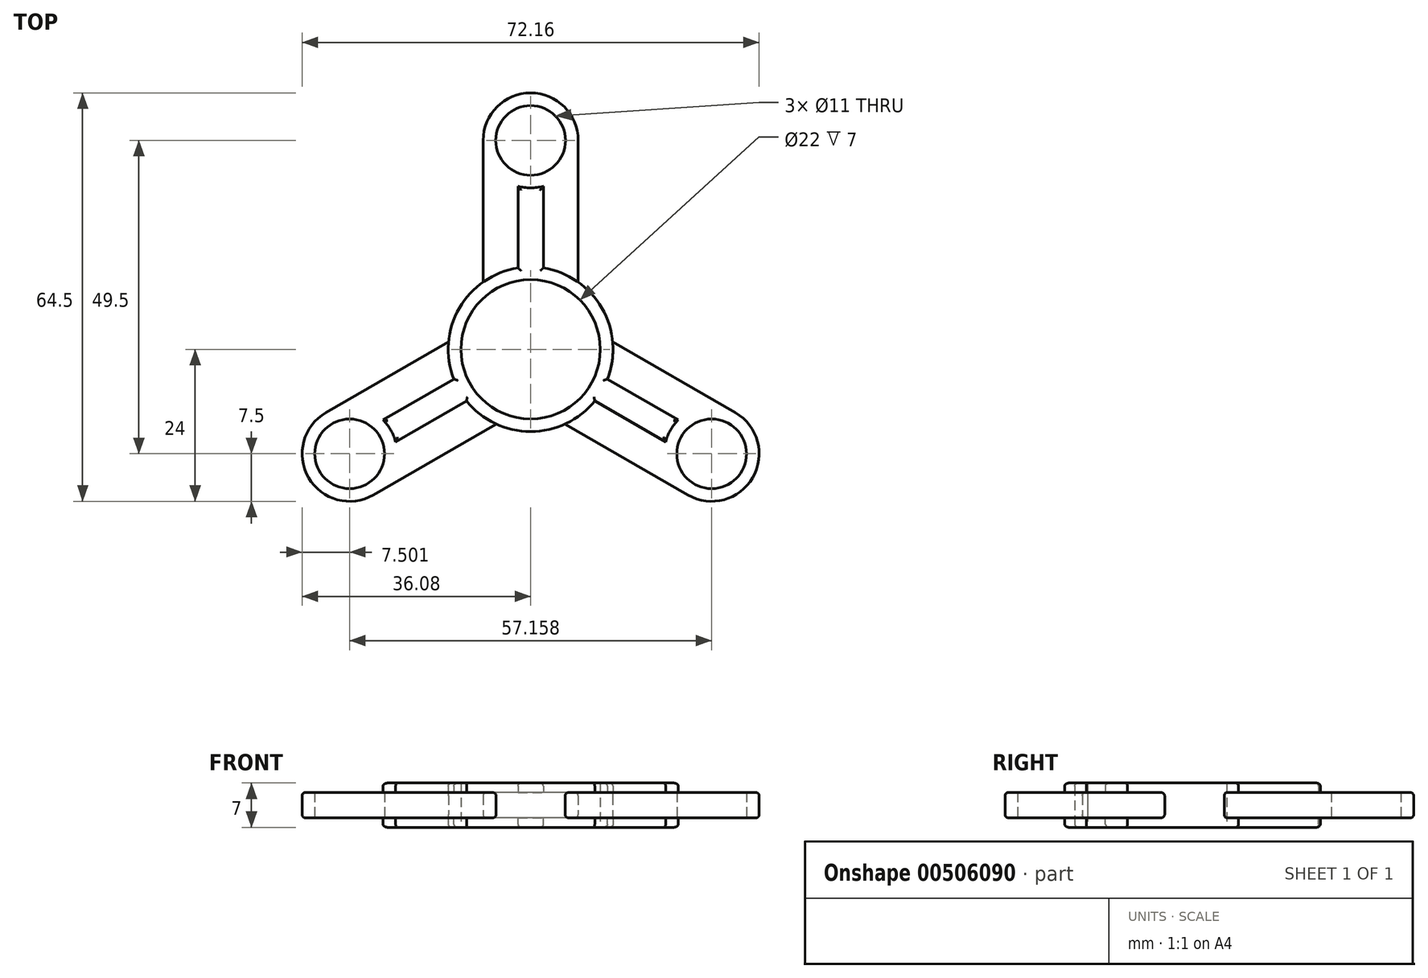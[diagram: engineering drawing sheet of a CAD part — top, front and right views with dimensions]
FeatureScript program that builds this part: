
annotation { "Feature Type Name" : "Feature", "Feature Type Description" : "" }
export const myFeature = defineFeature(function(context is Context, id is Id, definition is map)
    precondition{}
    {
        {
            var Q0;
            Q0=qCreatedBy(makeId("Top.planeOp"),FACE);
            var sketch = newSketch(context, id + "F0", { "sketchPlane" : qUnion([Q0])});
            skCircle(sketch, "E0", {"center": v(0, 0) * mm, "radius": 11 * mm});
            skCircle(sketch, "E1", {"center": v(0, 33) * mm, "radius": 5.5 * mm});
            skCircle(sketch, "E2", {"center": v(-28.58, -16.5) * mm, "radius": 5.5 * mm});
            skCircle(sketch, "E3", {"center": v(28.58, -16.5) * mm, "radius": 5.5 * mm});
            skCircle(sketch, "E4", {"center": v(0, 33) * mm, "radius": 7.5 * mm});
            skCircle(sketch, "E5", {"center": v(-28.58, -16.5) * mm, "radius": 7.5 * mm});
            skCircle(sketch, "E6", {"center": v(28.58, -16.5) * mm, "radius": 7.5 * mm});
            skCircle(sketch, "E7", {"center": v(0, 0) * mm, "radius": 13 * mm});
            skLineSegment(sketch, "E8", {"start": v(-7.5, 33) * mm, "end": v(-7.5, 10.62) * mm});
            skLineSegment(sketch, "E9", {"start": v(7.5, 33) * mm, "end": v(7.5, 10.62) * mm});
            skLineSegment(sketch, "E10", {"start": v(32.33, -10) * mm, "end": v(12.95, 1.19) * mm});
            skLineSegment(sketch, "E11", {"start": v(24.83, -23) * mm, "end": v(5.45, -11.8) * mm});
            skLineSegment(sketch, "E12", {"start": v(-32.33, -10) * mm, "end": v(-12.95, 1.19) * mm});
            skLineSegment(sketch, "E13", {"start": v(-24.83, -23) * mm, "end": v(-5.45, -11.8) * mm});
            skLineSegment(sketch, "E14", {"start": v(-12.12, -4.7) * mm, "end": v(-23.32, -11.15) * mm});
            skLineSegment(sketch, "E15", {"start": v(-10.12, -8.15) * mm, "end": v(-21.32, -14.62) * mm});
            skLineSegment(sketch, "E16", {"start": v(12.12, -4.7) * mm, "end": v(23.32, -11.15) * mm});
            skLineSegment(sketch, "E17", {"start": v(21.32, -14.62) * mm, "end": v(10.12, -8.15) * mm});
            skLineSegment(sketch, "E18", {"start": v(-2, 25.77) * mm, "end": v(-2, 12.85) * mm});
            skLineSegment(sketch, "E19", {"start": v(2, 25.77) * mm, "end": v(2, 12.85) * mm});
            skSolve(sketch);
        }
        {
            var Q0;
            Q0=qSketchRegion(id+"F0",true);
            extrude(context, id + "F1", {"entities" : qUnion([Q0]), "depth" : 4 * mm});
        }
        {
            var Q0;
            {var subQ0=sQuery(id+"F0.wireOp",EDGE,"E14");Q0=makeQuery(id+"F0.imprint","IMPRINT",FACE,{"disambiguationData":[TD([[makeQuery(id+"F0.imprint","IMPRINT",EDGE,{"derivedFrom":subQ0}),1.0]])]});}
            var Q1;
            {var subQ0=sQuery(id+"F0.wireOp",EDGE,"E18");Q1=makeQuery(id+"F0.imprint","IMPRINT",FACE,{"disambiguationData":[TD([[makeQuery(id+"F0.imprint","IMPRINT",EDGE,{"derivedFrom":subQ0}),1.0]])]});}
            var Q2;
            {var subQ0=sQuery(id+"F0.wireOp",EDGE,"E16");Q2=makeQuery(id+"F0.imprint","IMPRINT",FACE,{"disambiguationData":[TD([[makeQuery(id+"F0.imprint","IMPRINT",EDGE,{"derivedFrom":subQ0}),-1.0]])]});}
            var Q3;
            Q3=makeQuery(id+"F0.imprint","IMPRINT",FACE,{"disambiguationData":[TD([[makeQuery(id+"F0.imprint","IMPRINT",EDGE,{"derivedFrom":sQuery(id+"F0.wireOp",EDGE,"E0")}),-1.0]])]});
            extrude(context, id + "F2", {"entities" : qUnion([Q0, Q1, Q2, Q3]), "operationType" : NewBodyOperationType.ADD, "depth" : 5.5 * mm});
        }
        {
            var Q0;
            {var subQ0=sQuery(id+"F0.wireOp",EDGE,"E14");Q0=makeQuery(id+"F0.imprint","IMPRINT",FACE,{"disambiguationData":[TD([[makeQuery(id+"F0.imprint","IMPRINT",EDGE,{"derivedFrom":subQ0}),1.0]])]});}
            var Q1;
            Q1=makeQuery(id+"F0.imprint","IMPRINT",FACE,{"disambiguationData":[TD([[makeQuery(id+"F0.imprint","IMPRINT",EDGE,{"derivedFrom":sQuery(id+"F0.wireOp",EDGE,"E0")}),-1.0]])]});
            var Q2;
            {var subQ0=sQuery(id+"F0.wireOp",EDGE,"E18");Q2=makeQuery(id+"F0.imprint","IMPRINT",FACE,{"disambiguationData":[TD([[makeQuery(id+"F0.imprint","IMPRINT",EDGE,{"derivedFrom":subQ0}),1.0]])]});}
            var Q3;
            {var subQ0=sQuery(id+"F0.wireOp",EDGE,"E16");Q3=makeQuery(id+"F0.imprint","IMPRINT",FACE,{"disambiguationData":[TD([[makeQuery(id+"F0.imprint","IMPRINT",EDGE,{"derivedFrom":subQ0}),-1.0]])]});}
            extrude(context, id + "F3", {"entities" : qUnion([Q0, Q1, Q2, Q3]), "operationType" : NewBodyOperationType.ADD, "oppositeDirection" : true, "depth" : 1.5 * mm});
        }
        {
            var Q0;
            Q0=makeQuery(id+"F2.opExtrude","CAP_EDGE",EDGE,{"disambiguationData":[OSD([sQuery(id+"F0.wireOp",EDGE,"E15")])],"isStart":false});
            var Q1;
            Q1=makeQuery(id+"F2.opExtrude","CAP_EDGE",EDGE,{"disambiguationData":[OSD([sQuery(id+"F0.wireOp",EDGE,"E14")])],"isStart":false});
            var Q2;
            Q2=makeQuery(id+"F2.opExtrude","CAP_EDGE",EDGE,{"disambiguationData":[OSD([sQuery(id+"F0.wireOp",EDGE,"E5")])],"isStart":false});
            var Q3;
            Q3=makeQuery(id+"F2.opExtrude","CAP_EDGE",EDGE,{"disambiguationData":[OSD([sQuery(id+"F0.wireOp",EDGE,"E17")])],"isStart":false});
            var Q4;
            Q4=makeQuery(id+"F2.opExtrude","CAP_EDGE",EDGE,{"disambiguationData":[OSD([sQuery(id+"F0.wireOp",EDGE,"E16")])],"isStart":false});
            var Q5;
            Q5=makeQuery(id+"F2.opExtrude","CAP_EDGE",EDGE,{"disambiguationData":[OSD([sQuery(id+"F0.wireOp",EDGE,"E6")])],"isStart":false});
            var Q6;
            Q6=makeQuery(id+"F2.opExtrude","CAP_EDGE",EDGE,{"disambiguationData":[OSD([sQuery(id+"F0.wireOp",EDGE,"E18")])],"isStart":false});
            var Q7;
            Q7=makeQuery(id+"F2.opExtrude","CAP_EDGE",EDGE,{"disambiguationData":[OSD([sQuery(id+"F0.wireOp",EDGE,"E19")])],"isStart":false});
            var Q8;
            Q8=makeQuery(id+"F2.opExtrude","CAP_EDGE",EDGE,{"disambiguationData":[OSD([sQuery(id+"F0.wireOp",EDGE,"E4")])],"isStart":false});
            fillet(context, id + "F4", {"entities" : qUnion([Q0, Q1, Q2, Q3, Q4, Q5, Q6, Q7, Q8]), "radius" : .5 * mm, "tangentPropagation" : true, "allowEdgeOverflow" : false});
        }
        {
            var Q0;
            {var subQ0=sQuery(id+"F0.wireOp",EDGE,"E7");var subQ1=makeQuery(id+"F0.imprint","INTERSECT",VERTEX,{"derivedFrom":[subQ0,sQuery(id+"F0.wireOp",EDGE,"E12")]});var subQ2=makeQuery(id+"F0.imprint","INTERSECT",VERTEX,{"derivedFrom":[subQ0,sQuery(id+"F0.wireOp",EDGE,"E8")]});Q0=makeQuery(id+"F2.opExtrude","CAP_EDGE",EDGE,{"disambiguationData":[OSD([subQ0]),TDD([makeQuery(id+"F0.imprint","IMPRINT",EDGE,{"disambiguationData":[TD([[subQ2,1.0]])],"derivedFrom":subQ0}),makeQuery(id+"F0.imprint","IMPRINT",EDGE,{"disambiguationData":[TD([[subQ2,-1.0]])],"derivedFrom":subQ0}),makeQuery(id+"F0.imprint","IMPRINT",EDGE,{"disambiguationData":[TD([[subQ1,-1.0]])],"derivedFrom":subQ0})])],"isStart":false});}
            var Q1;
            {var subQ0=sQuery(id+"F0.wireOp",EDGE,"E7");var subQ1=makeQuery(id+"F0.imprint","INTERSECT",VERTEX,{"derivedFrom":[subQ0,sQuery(id+"F0.wireOp",EDGE,"E11")]});var subQ2=makeQuery(id+"F0.imprint","INTERSECT",VERTEX,{"derivedFrom":[subQ0,sQuery(id+"F0.wireOp",EDGE,"E13")]});Q1=makeQuery(id+"F2.opExtrude","CAP_EDGE",EDGE,{"disambiguationData":[OSD([subQ0]),TDD([makeQuery(id+"F0.imprint","IMPRINT",EDGE,{"disambiguationData":[TD([[subQ2,1.0]])],"derivedFrom":subQ0}),makeQuery(id+"F0.imprint","IMPRINT",EDGE,{"disambiguationData":[TD([[subQ1,1.0]])],"derivedFrom":subQ0}),makeQuery(id+"F0.imprint","IMPRINT",EDGE,{"disambiguationData":[TD([[subQ1,-1.0]])],"derivedFrom":subQ0})])],"isStart":false});}
            var Q2;
            {var subQ0=sQuery(id+"F0.wireOp",EDGE,"E7");var subQ1=makeQuery(id+"F0.imprint","INTERSECT",VERTEX,{"derivedFrom":[subQ0,sQuery(id+"F0.wireOp",EDGE,"E10")]});var subQ2=makeQuery(id+"F0.imprint","INTERSECT",VERTEX,{"derivedFrom":[subQ0,sQuery(id+"F0.wireOp",EDGE,"E9")]});Q2=makeQuery(id+"F2.opExtrude","CAP_EDGE",EDGE,{"disambiguationData":[OSD([subQ0]),TDD([makeQuery(id+"F0.imprint","IMPRINT",EDGE,{"disambiguationData":[TD([[subQ2,1.0]])],"derivedFrom":subQ0}),makeQuery(id+"F0.imprint","IMPRINT",EDGE,{"disambiguationData":[TD([[subQ2,-1.0]])],"derivedFrom":subQ0}),makeQuery(id+"F0.imprint","IMPRINT",EDGE,{"disambiguationData":[TD([[subQ1,1.0]])],"derivedFrom":subQ0})])],"isStart":false});}
            fillet(context, id + "F5", {"entities" : qUnion([Q0, Q1, Q2]), "radius" : .5 * mm, "tangentPropagation" : true, "allowEdgeOverflow" : false});
        }
        {
            var Q0;
            Q0=makeQuery(id+"F1.opExtrude","CAP_EDGE",EDGE,{"disambiguationData":[OSD([sQuery(id+"F0.wireOp",EDGE,"E8")])],"isStart":false});
            var Q1;
            {var subQ0=sQuery(id+"F0.wireOp",EDGE,"E4");Q1=makeQuery(id+"F1.opExtrude","CAP_EDGE",EDGE,{"disambiguationData":[OSD([subQ0]),TDD([makeQuery(id+"F0.imprint","IMPRINT",EDGE,{"disambiguationData":[TD([[makeQuery(id+"F0.imprint","INTERSECT",VERTEX,{"derivedFrom":[subQ0,sQuery(id+"F0.wireOp",EDGE,"E8")]}),1.0]])],"derivedFrom":subQ0})])],"isStart":false});}
            var Q2;
            Q2=makeQuery(id+"F1.opExtrude","CAP_EDGE",EDGE,{"disambiguationData":[OSD([sQuery(id+"F0.wireOp",EDGE,"E9")])],"isStart":false});
            var Q3;
            Q3=makeQuery(id+"F1.opExtrude","CAP_EDGE",EDGE,{"disambiguationData":[OSD([sQuery(id+"F0.wireOp",EDGE,"E12")])],"isStart":false});
            var Q4;
            {var subQ0=sQuery(id+"F0.wireOp",EDGE,"E5");Q4=makeQuery(id+"F1.opExtrude","CAP_EDGE",EDGE,{"disambiguationData":[OSD([subQ0]),TDD([makeQuery(id+"F0.imprint","IMPRINT",EDGE,{"disambiguationData":[TD([[makeQuery(id+"F0.imprint","INTERSECT",VERTEX,{"derivedFrom":[subQ0,sQuery(id+"F0.wireOp",EDGE,"E12")]}),-1.0]])],"derivedFrom":subQ0})])],"isStart":false});}
            var Q5;
            Q5=makeQuery(id+"F1.opExtrude","CAP_EDGE",EDGE,{"disambiguationData":[OSD([sQuery(id+"F0.wireOp",EDGE,"E13")])],"isStart":false});
            var Q6;
            Q6=makeQuery(id+"F1.opExtrude","CAP_EDGE",EDGE,{"disambiguationData":[OSD([sQuery(id+"F0.wireOp",EDGE,"E11")])],"isStart":false});
            var Q7;
            {var subQ0=sQuery(id+"F0.wireOp",EDGE,"E6");Q7=makeQuery(id+"F1.opExtrude","CAP_EDGE",EDGE,{"disambiguationData":[OSD([subQ0]),TDD([makeQuery(id+"F0.imprint","IMPRINT",EDGE,{"disambiguationData":[TD([[makeQuery(id+"F0.imprint","INTERSECT",VERTEX,{"derivedFrom":[subQ0,sQuery(id+"F0.wireOp",EDGE,"E10")]}),1.0]])],"derivedFrom":subQ0})])],"isStart":false});}
            var Q8;
            Q8=makeQuery(id+"F1.opExtrude","CAP_EDGE",EDGE,{"disambiguationData":[OSD([sQuery(id+"F0.wireOp",EDGE,"E10")])],"isStart":false});
            fillet(context, id + "F6", {"entities" : qUnion([Q0, Q1, Q2, Q3, Q4, Q5, Q6, Q7, Q8]), "radius" : .5 * mm, "tangentPropagation" : true, "allowEdgeOverflow" : false});
        }
        {
            var Q0;
            Q0=makeQuery(id+"F3.opExtrude","CAP_EDGE",EDGE,{"disambiguationData":[OSD([sQuery(id+"F0.wireOp",EDGE,"E16")])],"isStart":false});
            var Q1;
            Q1=makeQuery(id+"F3.opExtrude","CAP_EDGE",EDGE,{"disambiguationData":[OSD([sQuery(id+"F0.wireOp",EDGE,"E6")])],"isStart":false});
            var Q2;
            Q2=makeQuery(id+"F3.opExtrude","CAP_EDGE",EDGE,{"disambiguationData":[OSD([sQuery(id+"F0.wireOp",EDGE,"E17")])],"isStart":false});
            var Q3;
            {var subQ0=sQuery(id+"F0.wireOp",EDGE,"E7");var subQ1=makeQuery(id+"F0.imprint","INTERSECT",VERTEX,{"derivedFrom":[subQ0,sQuery(id+"F0.wireOp",EDGE,"E11")]});var subQ2=makeQuery(id+"F0.imprint","INTERSECT",VERTEX,{"derivedFrom":[subQ0,sQuery(id+"F0.wireOp",EDGE,"E13")]});Q3=makeQuery(id+"F3.opExtrude","CAP_EDGE",EDGE,{"disambiguationData":[OSD([subQ0]),TDD([makeQuery(id+"F0.imprint","IMPRINT",EDGE,{"disambiguationData":[TD([[subQ2,1.0]])],"derivedFrom":subQ0}),makeQuery(id+"F0.imprint","IMPRINT",EDGE,{"disambiguationData":[TD([[subQ1,1.0]])],"derivedFrom":subQ0}),makeQuery(id+"F0.imprint","IMPRINT",EDGE,{"disambiguationData":[TD([[subQ1,-1.0]])],"derivedFrom":subQ0})])],"isStart":false});}
            var Q4;
            {var subQ0=sQuery(id+"F0.wireOp",EDGE,"E7");var subQ1=makeQuery(id+"F0.imprint","INTERSECT",VERTEX,{"derivedFrom":[subQ0,sQuery(id+"F0.wireOp",EDGE,"E12")]});var subQ2=makeQuery(id+"F0.imprint","INTERSECT",VERTEX,{"derivedFrom":[subQ0,sQuery(id+"F0.wireOp",EDGE,"E8")]});Q4=makeQuery(id+"F3.opExtrude","CAP_EDGE",EDGE,{"disambiguationData":[OSD([subQ0]),TDD([makeQuery(id+"F0.imprint","IMPRINT",EDGE,{"disambiguationData":[TD([[subQ2,1.0]])],"derivedFrom":subQ0}),makeQuery(id+"F0.imprint","IMPRINT",EDGE,{"disambiguationData":[TD([[subQ2,-1.0]])],"derivedFrom":subQ0}),makeQuery(id+"F0.imprint","IMPRINT",EDGE,{"disambiguationData":[TD([[subQ1,-1.0]])],"derivedFrom":subQ0})])],"isStart":false});}
            var Q5;
            {var subQ0=sQuery(id+"F0.wireOp",EDGE,"E7");var subQ1=makeQuery(id+"F0.imprint","INTERSECT",VERTEX,{"derivedFrom":[subQ0,sQuery(id+"F0.wireOp",EDGE,"E10")]});var subQ2=makeQuery(id+"F0.imprint","INTERSECT",VERTEX,{"derivedFrom":[subQ0,sQuery(id+"F0.wireOp",EDGE,"E9")]});Q5=makeQuery(id+"F3.opExtrude","CAP_EDGE",EDGE,{"disambiguationData":[OSD([subQ0]),TDD([makeQuery(id+"F0.imprint","IMPRINT",EDGE,{"disambiguationData":[TD([[subQ2,1.0]])],"derivedFrom":subQ0}),makeQuery(id+"F0.imprint","IMPRINT",EDGE,{"disambiguationData":[TD([[subQ2,-1.0]])],"derivedFrom":subQ0}),makeQuery(id+"F0.imprint","IMPRINT",EDGE,{"disambiguationData":[TD([[subQ1,1.0]])],"derivedFrom":subQ0})])],"isStart":false});}
            var Q6;
            Q6=makeQuery(id+"F3.opExtrude","CAP_EDGE",EDGE,{"disambiguationData":[OSD([sQuery(id+"F0.wireOp",EDGE,"E15")])],"isStart":false});
            var Q7;
            Q7=makeQuery(id+"F3.opExtrude","CAP_EDGE",EDGE,{"disambiguationData":[OSD([sQuery(id+"F0.wireOp",EDGE,"E5")])],"isStart":false});
            var Q8;
            Q8=makeQuery(id+"F3.opExtrude","CAP_EDGE",EDGE,{"disambiguationData":[OSD([sQuery(id+"F0.wireOp",EDGE,"E14")])],"isStart":false});
            var Q9;
            Q9=makeQuery(id+"F1.opExtrude","CAP_EDGE",EDGE,{"disambiguationData":[OSD([sQuery(id+"F0.wireOp",EDGE,"E10")])],"isStart":true});
            var Q10;
            {var subQ0=sQuery(id+"F0.wireOp",EDGE,"E6");Q10=makeQuery(id+"F1.opExtrude","CAP_EDGE",EDGE,{"disambiguationData":[OSD([subQ0]),TDD([makeQuery(id+"F0.imprint","IMPRINT",EDGE,{"disambiguationData":[TD([[makeQuery(id+"F0.imprint","INTERSECT",VERTEX,{"derivedFrom":[subQ0,sQuery(id+"F0.wireOp",EDGE,"E10")]}),1.0]])],"derivedFrom":subQ0})])],"isStart":true});}
            var Q11;
            Q11=makeQuery(id+"F1.opExtrude","CAP_EDGE",EDGE,{"disambiguationData":[OSD([sQuery(id+"F0.wireOp",EDGE,"E11")])],"isStart":true});
            var Q12;
            Q12=makeQuery(id+"F1.opExtrude","CAP_EDGE",EDGE,{"disambiguationData":[OSD([sQuery(id+"F0.wireOp",EDGE,"E13")])],"isStart":true});
            var Q13;
            Q13=makeQuery(id+"F1.opExtrude","CAP_EDGE",EDGE,{"disambiguationData":[OSD([sQuery(id+"F0.wireOp",EDGE,"E12")])],"isStart":true});
            var Q14;
            {var subQ0=sQuery(id+"F0.wireOp",EDGE,"E5");Q14=makeQuery(id+"F1.opExtrude","CAP_EDGE",EDGE,{"disambiguationData":[OSD([subQ0]),TDD([makeQuery(id+"F0.imprint","IMPRINT",EDGE,{"disambiguationData":[TD([[makeQuery(id+"F0.imprint","INTERSECT",VERTEX,{"derivedFrom":[subQ0,sQuery(id+"F0.wireOp",EDGE,"E12")]}),-1.0]])],"derivedFrom":subQ0})])],"isStart":true});}
            var Q15;
            Q15=makeQuery(id+"F3.opExtrude","CAP_EDGE",EDGE,{"disambiguationData":[OSD([sQuery(id+"F0.wireOp",EDGE,"E19")])],"isStart":false});
            var Q16;
            Q16=makeQuery(id+"F3.opExtrude","CAP_EDGE",EDGE,{"disambiguationData":[OSD([sQuery(id+"F0.wireOp",EDGE,"E18")])],"isStart":false});
            var Q17;
            Q17=makeQuery(id+"F3.opExtrude","CAP_EDGE",EDGE,{"disambiguationData":[OSD([sQuery(id+"F0.wireOp",EDGE,"E4")])],"isStart":false});
            var Q18;
            Q18=makeQuery(id+"F1.opExtrude","CAP_EDGE",EDGE,{"disambiguationData":[OSD([sQuery(id+"F0.wireOp",EDGE,"E8")])],"isStart":true});
            var Q19;
            {var subQ0=sQuery(id+"F0.wireOp",EDGE,"E4");Q19=makeQuery(id+"F1.opExtrude","CAP_EDGE",EDGE,{"disambiguationData":[OSD([subQ0]),TDD([makeQuery(id+"F0.imprint","IMPRINT",EDGE,{"disambiguationData":[TD([[makeQuery(id+"F0.imprint","INTERSECT",VERTEX,{"derivedFrom":[subQ0,sQuery(id+"F0.wireOp",EDGE,"E8")]}),1.0]])],"derivedFrom":subQ0})])],"isStart":true});}
            var Q20;
            Q20=makeQuery(id+"F1.opExtrude","CAP_EDGE",EDGE,{"disambiguationData":[OSD([sQuery(id+"F0.wireOp",EDGE,"E9")])],"isStart":true});
            fillet(context, id + "F7", {"entities" : qUnion([Q0, Q1, Q2, Q3, Q4, Q5, Q6, Q7, Q8, Q9, Q10, Q11, Q12, Q13, Q14, Q15, Q16, Q17, Q18, Q19, Q20]), "radius" : .5 * mm, "tangentPropagation" : true, "allowEdgeOverflow" : false});
        }
    });
